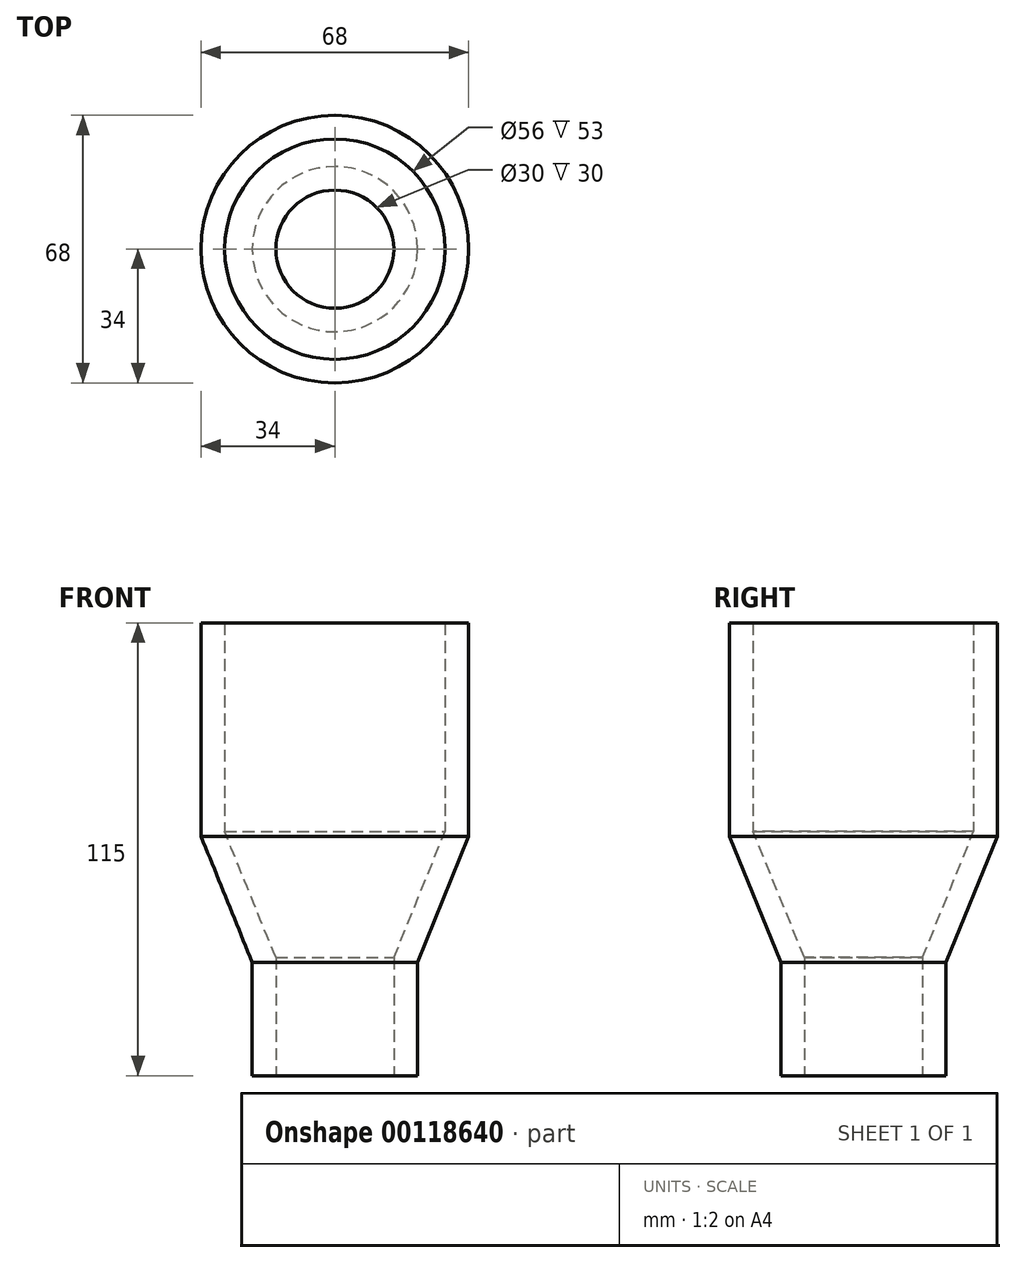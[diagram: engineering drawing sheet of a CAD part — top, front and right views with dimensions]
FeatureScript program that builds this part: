
annotation { "Feature Type Name" : "Feature", "Feature Type Description" : "" }
export const myFeature = defineFeature(function(context is Context, id is Id, definition is map)
    precondition{}
    {
        {
            var Q0;
            Q0=qCreatedBy(makeId("Front.planeOp"),FACE);
            var sketch = newSketch(context, id + "F0", { "sketchPlane" : qUnion([Q0])});
            skLineSegment(sketch, "E0", {"start": v(0, 0) * mm, "end": v(0, 124.26) * mm, "construction": true});
            skLineSegment(sketch, "E1", {"start": v(15, 0) * mm, "end": v(15, 30) * mm});
            skLineSegment(sketch, "E2", {"start": v(15, 30) * mm, "end": v(28, 62) * mm});
            skLineSegment(sketch, "E3", {"start": v(28, 62) * mm, "end": v(28, 115) * mm});
            skLineSegment(sketch, "E4.0", {"start": v(21, 0) * mm, "end": v(21, 28.83) * mm});
            skLineSegment(sketch, "E5.0", {"start": v(21, 28.83) * mm, "end": v(34, 60.83) * mm});
            skLineSegment(sketch, "E6.0", {"start": v(34, 60.83) * mm, "end": v(34, 115) * mm});
            skLineSegment(sketch, "E7", {"start": v(21, 0) * mm, "end": v(15, 0) * mm});
            skLineSegment(sketch, "E8", {"start": v(28, 115) * mm, "end": v(34, 115) * mm});
            skSolve(sketch);
        }
        {
            var Q0;
            Q0 = qSketchRegion(id + "F0", true);
            var Q1;
            Q1=sQuery(id+"F0.wireOp",EDGE,"E0");
            revolve(context, id + "F1", {"entities" : qUnion([Q0]), "axis" : qUnion([Q1]), "revolveType" : RevolveType.FULL});
        }
    });
